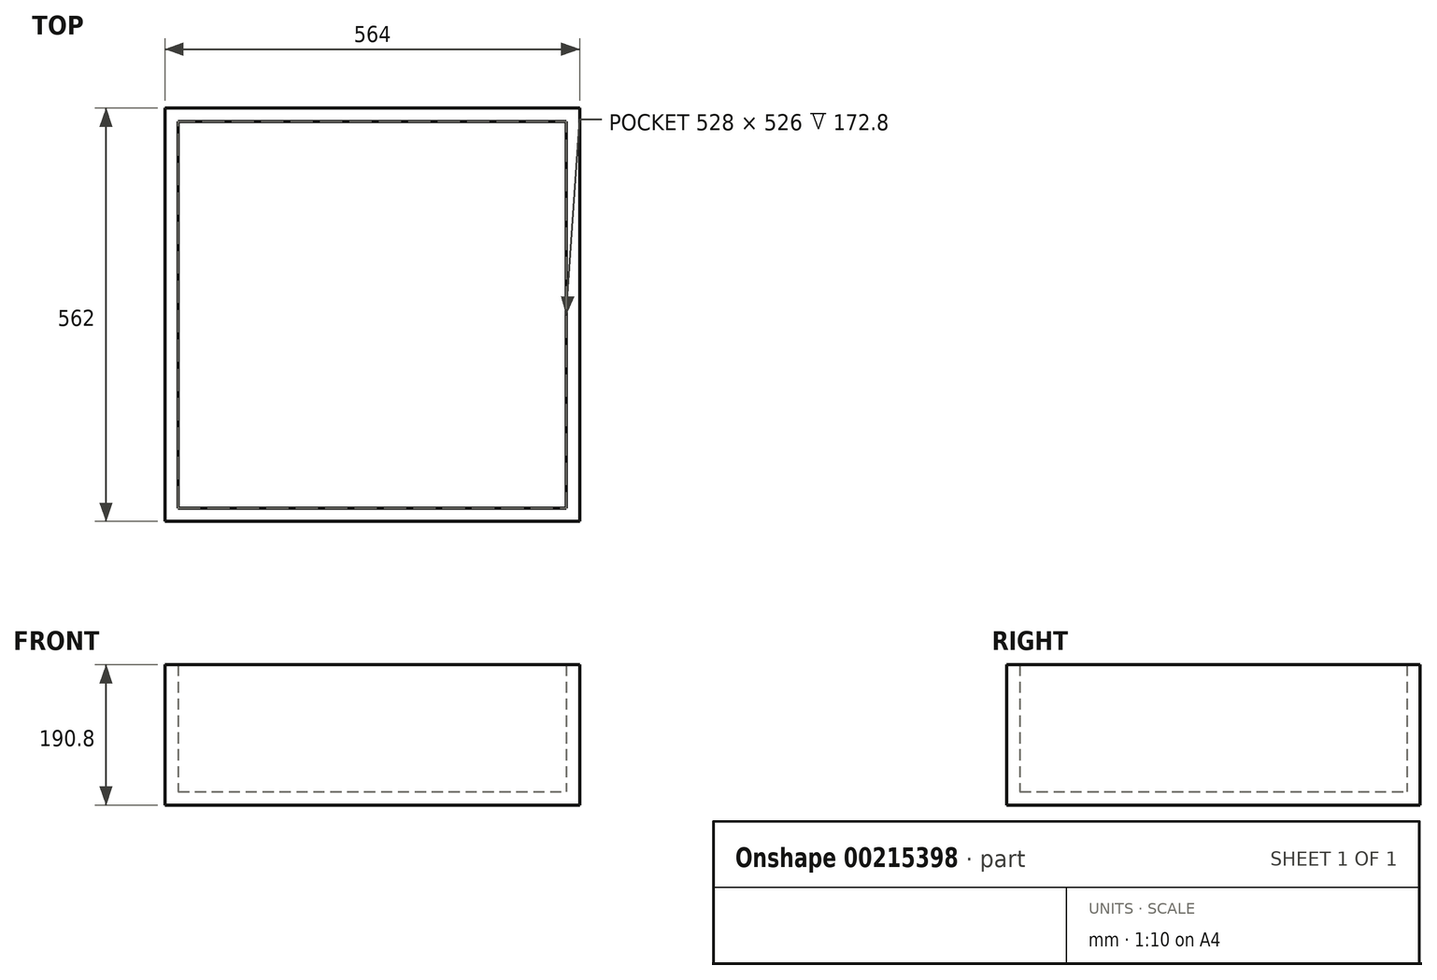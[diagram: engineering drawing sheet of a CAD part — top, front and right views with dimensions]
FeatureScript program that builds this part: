
annotation { "Feature Type Name" : "Feature", "Feature Type Description" : "" }
export const myFeature = defineFeature(function(context is Context, id is Id, definition is map)
    precondition{}
    {
        {
            var Q0;
            Q0=qCreatedBy(makeId("Top.planeOp"),FACE);
            var sketch = newSketch(context, id + "F0", { "sketchPlane" : qUnion([Q0])});
            skLineSegment(sketch, "E0.bottom", {"start": v(-282, -281) * mm, "end": v(282, -281) * mm});
            skLineSegment(sketch, "E0.top", {"start": v(-282, 281) * mm, "end": v(282, 281) * mm});
            skLineSegment(sketch, "E0.left", {"start": v(-282, -281) * mm, "end": v(-282, 281) * mm});
            skLineSegment(sketch, "E0.right", {"start": v(282, -281) * mm, "end": v(282, 281) * mm});
            skPoint(sketch, "E0.middle", {"position": v(0, 0) * mm});
            skSolve(sketch);
        }
        {
            var Q0;
            Q0=makeQuery(id+"F0.imprint","IMPRINT",FACE,{"disambiguationData":[TD([[makeQuery(id+"F0.imprint","IMPRINT",EDGE,{"derivedFrom":sQuery(id+"F0.wireOp",EDGE,"E0.bottom")}),1.0]])]});
            extrude(context, id + "F1", {"entities" : qUnion([Q0]), "flatOperationType" : FlatOperationType.REMOVE, "offsetDistance" : 25 * mm, "depth" : 190.8 * mm, "domain" : OperationDomain.MODEL});
        }
        {
            var Q0;
            Q0=makeQuery(id+"F1.opExtrude","CAP_FACE",FACE,{"disambiguationData":[OSD([sQuery(id+"F0.wireOp",EDGE,"E0.bottom"),sQuery(id+"F0.wireOp",EDGE,"E0.top"),sQuery(id+"F0.wireOp",EDGE,"E0.left"),sQuery(id+"F0.wireOp",EDGE,"E0.right")])],"isStart":false});
            shell(context, id + "F2", {"entities" : qUnion([Q0]), "thickness" : 18 * mm});
        }
    });
